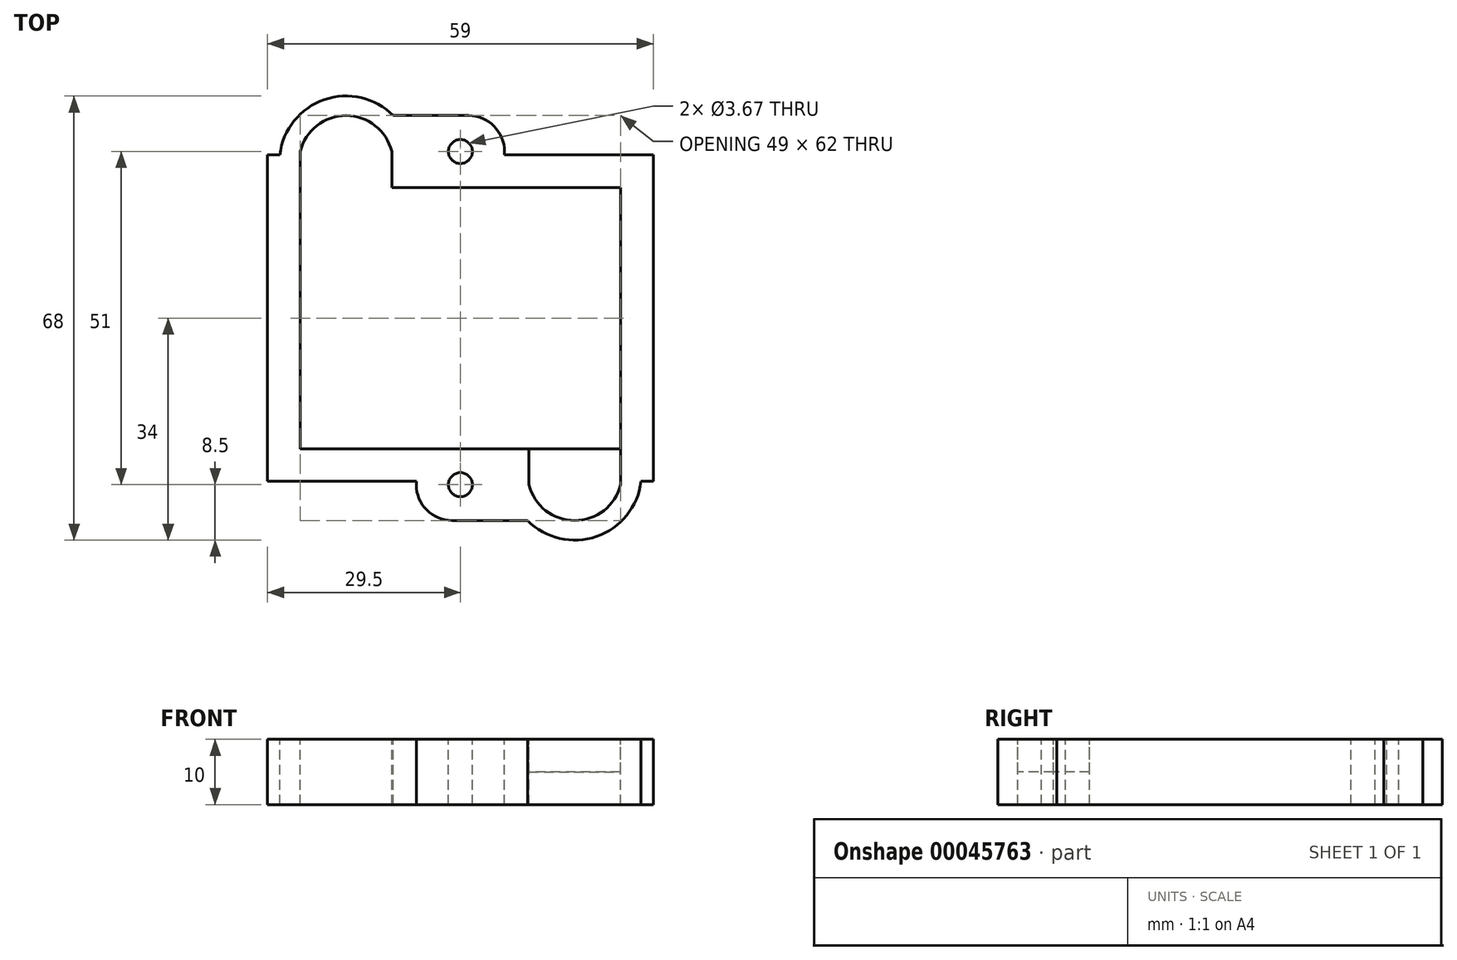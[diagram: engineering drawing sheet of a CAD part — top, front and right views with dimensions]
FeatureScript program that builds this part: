
annotation { "Feature Type Name" : "Feature", "Feature Type Description" : "" }
export const myFeature = defineFeature(function(context is Context, id is Id, definition is map)
    precondition{}
    {
        {
            var Q0;
            Q0=qCreatedBy(makeId("Top.planeOp"),FACE);
            var sketch = newSketch(context, id + "F1", { "sketchPlane" : qUnion([Q0])});
            skLineSegment(sketch, "E0.rect.bottom", {"start": v(24.5, 20) * mm, "end": v(-24.5, 20) * mm});
            skLineSegment(sketch, "E0.rect.top", {"start": v(24.5, -20) * mm, "end": v(-24.5, -20) * mm});
            skLineSegment(sketch, "E0.rect.left", {"start": v(24.5, 20) * mm, "end": v(24.5, -20) * mm});
            skLineSegment(sketch, "E0.rect.right", {"start": v(-24.5, 20) * mm, "end": v(-24.5, -20) * mm});
            skPoint(sketch, "E0.rect.middle", {"position": v(0, 0) * mm});
            skLineSegment(sketch, "E1.bottom", {"start": v(-24.5, 20) * mm, "end": v(-10.5, 20) * mm});
            skLineSegment(sketch, "E1.left", {"start": v(-24.5, 20) * mm, "end": v(-24.5, 25.5) * mm});
            skLineSegment(sketch, "E1.right", {"start": v(-10.5, 20) * mm, "end": v(-10.5, 25.5) * mm});
            skLineSegment(sketch, "E2.bottom", {"start": v(24.5, -20) * mm, "end": v(10.5, -20) * mm});
            skLineSegment(sketch, "E2.left", {"start": v(24.5, -20) * mm, "end": v(24.5, -25.5) * mm});
            skLineSegment(sketch, "E2.right", {"start": v(10.5, -20) * mm, "end": v(10.5, -25.5) * mm});
            skPoint(sketch, "E3.first.point", {"position": v(-24.5, 25.5) * mm});
            skPoint(sketch, "E3.second.point", {"position": v(-10.5, 25.5) * mm});
            skPoint(sketch, "E3.third.point", {"position": v(-17.5, 31) * mm});
            skArc(sketch, "E4.trimOffspring", {"start": v(-10.5, 25.5) * mm, "mid": v(-17.5, 31) * mm, "end": v(-24.5, 25.5) * mm});
            skLineSegment(sketch, "E5", {"start": v(-24.5, 0) * mm, "end": v(24.5, 0) * mm, "construction": true});
            skLineSegment(sketch, "E6.MirrorCS", {"start": v(24.5, -20) * mm, "end": v(24.5, 20) * mm});
            skPoint(sketch, "E7.first.point", {"position": v(24.5, -25.5) * mm});
            skPoint(sketch, "E7.second.point", {"position": v(10.5, -25.5) * mm});
            skArc(sketch, "E8.trimOffspring", {"start": v(10.5, -25.5) * mm, "mid": v(17.5, -31) * mm, "end": v(24.5, -25.5) * mm});
            skLineSegment(sketch, "E9", {"start": v(0, 0) * mm, "end": v(0, 20) * mm, "construction": true});
            skLineSegment(sketch, "E10", {"start": v(0, 0) * mm, "end": v(0, -20) * mm, "construction": true});
            skLineSegment(sketch, "E11", {"start": v(6.75, 25) * mm, "end": v(6.75, 25.5) * mm});
            skArc(sketch, "E12", {"start": v(6.75, 25.5) * mm, "mid": v(5.14, 29.39) * mm, "end": v(1.25, 31) * mm});
            skLineSegment(sketch, "E13", {"start": v(1.25, 31) * mm, "end": v(-10.27, 31) * mm});
            skLineSegment(sketch, "E14.bottom", {"start": v(0, -20) * mm, "end": v(-6.75, -20) * mm});
            skLineSegment(sketch, "E14.top", {"start": v(0, -31) * mm, "end": v(-1.25, -31) * mm});
            skLineSegment(sketch, "E14.right", {"start": v(-6.75, -25) * mm, "end": v(-6.75, -25.5) * mm});
            skLineSegment(sketch, "E15", {"start": v(0, -31) * mm, "end": v(10.27, -31) * mm});
            skPoint(sketch, "E16.third.point", {"position": v(-1.25, -31) * mm});
            skArc(sketch, "E17.trimOffspring", {"start": v(-6.75, -25.5) * mm, "mid": v(-5.14, -29.39) * mm, "end": v(-1.25, -31) * mm});
            skLineSegment(sketch, "E18.rect.bottom", {"start": v(29.5, 25) * mm, "end": v(6.75, 25) * mm});
            skLineSegment(sketch, "E18.rect.top", {"start": v(29.5, -25) * mm, "end": v(27.63, -25) * mm});
            skLineSegment(sketch, "E18.rect.left", {"start": v(29.5, 25) * mm, "end": v(29.5, -25) * mm});
            skLineSegment(sketch, "E18.rect.right", {"start": v(-29.5, 25) * mm, "end": v(-29.5, -25) * mm});
            skArc(sketch, "E19", {"start": v(-10.27, 31) * mm, "mid": v(-20.83, 33.44) * mm, "end": v(-27.63, 25) * mm});
            skLineSegment(sketch, "E20.trimOffspring", {"start": v(-27.63, 25) * mm, "end": v(-29.5, 25) * mm});
            skArc(sketch, "E21", {"start": v(10.27, -31) * mm, "mid": v(20.83, -33.44) * mm, "end": v(27.63, -25) * mm});
            skLineSegment(sketch, "E22.trimOffspring", {"start": v(-6.75, -25) * mm, "end": v(-29.5, -25) * mm});
            skPoint(sketch, "E23.orphan", {"position": v(17.5, -31) * mm});
            skLineSegment(sketch, "E24", {"start": v(0, -20) * mm, "end": v(0, -40.88) * mm, "construction": true});
            skCircle(sketch, "E25", {"center": v(0, -25.5) * mm, "radius": 1.84 * mm});
            skLineSegment(sketch, "E26", {"start": v(0, 20) * mm, "end": v(0, 37.63) * mm, "construction": true});
            skCircle(sketch, "E27", {"center": v(0, 25.5) * mm, "radius": 1.84 * mm});
            skLineSegment(sketch, "E28", {"start": v(0, 25.5) * mm, "end": v(0, -25.5) * mm});
            skSolve(sketch);
        }
        {
            var Q0;
            Q0=makeQuery(id+"F1.imprint","IMPRINT",FACE,{"disambiguationData":[TD([[makeQuery(id+"F1.imprint","IMPRINT",EDGE,{"derivedFrom":sQuery(id+"F1.wireOp",EDGE,"E0.rect.bottom")}),-1.0]])]});
            extrude(context, id + "F0", {"entities" : qUnion([Q0]), "oppositeDirection" : true, "depth" : 10 * mm});
        }
        {
            var Q0;
            Q0=makeQuery(id+"F1.imprint","IMPRINT",FACE,{"disambiguationData":[TD([[makeQuery(id+"F1.imprint","IMPRINT",EDGE,{"derivedFrom":sQuery(id+"F1.wireOp",EDGE,"E1.bottom")}),1.0]])]});
            var Q1;
            {var subQ2=sQuery(id+"F1.wireOp",EDGE,"E2.left");Q1=makeQuery(id+"F1.imprint","IMPRINT",FACE,{"disambiguationData":[TD([[makeQuery(id+"F1.imprint","IMPRINT",EDGE,{"derivedFrom":subQ2}),-1.0]])]});}
            extrude(context, id + "F2", {"entities" : qUnion([Q0, Q1]), "oppositeDirection" : true, "depth" : 5 * mm});
        }
    });
